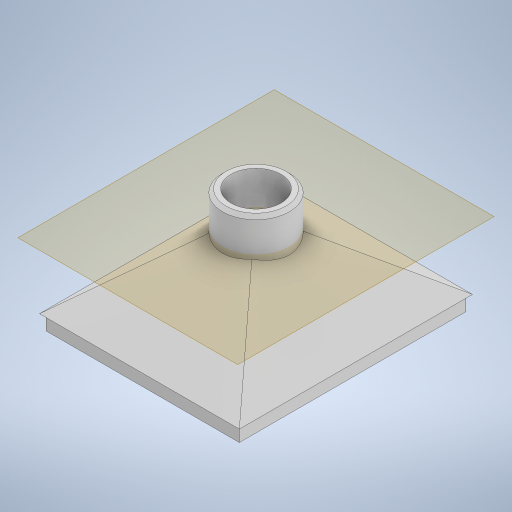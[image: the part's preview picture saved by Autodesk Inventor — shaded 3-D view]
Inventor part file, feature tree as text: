
AUTODESK INVENTOR PART (.ipt)
format: ipt  version: 2023 (Build 270158000, 158)  size: 410,624 bytes
history: native  units: mm
features: sketch x7, extrude x4, chamfer x2, plane x1, loft x1, hole x1, shell x1, fillet x1
ambient origin geometry x8: Origin, YZ Plane, XZ Plane, XY Plane, X Axis, Y Axis, Z Axis, Center Point
bodies: Solid1 (feature_tree)
feature tree (18):
  sketch  "Sketch1"  dims[d0=60.0mm d1=70.0mm]
  plane  "Work Plane1"
  loft  "Loft1"
  hole  "Hole1"  [1 undecoded]
  sketch  "Sketch10"  dims[d9=15.0mm d10=6.0mm d11=4.0mm d12=2.0mm d13=90.0deg d14=8.0mm d15=20.594885mm d16=1.0mm]
  shell  "Shell1"  Thickness=0.0mm
  extrude  "Extrusion1"  Depth=1.0mm
  extrude  "Extrusion2"  Depth=1.0mm
  fillet  "Fillet2"  Radius=1.0mm
  chamfer  "Chamfer1"  Distance=5.0mm
  extrude  "Extrusion3"  Depth=10.0mm
  extrude  "Extrusion4"  Depth=10.0mm
  chamfer  "Chamfer2"  Distance=1.0mm
  sketch  "Sketch2"  dims[d2=20.0mm d3=15.0mm d4=0.0mm d5=90.0deg]
  sketch  "Sketch6"  dims[d6=0.0mm d7=90.0deg]
  sketch  "Sketch12"  dims[d20=1.0mm d21=1.0mm d22=1.0mm]
  sketch  "Sketch13"  dims[d23=1.0mm d24=5.0mm d25=0.0mm]
  sketch  "Sketch14"  dims[d26=1.0mm d27=1.0mm d28=1.0mm d29=1.0mm d30=5.0mm d31=0.0mm d32=10.0mm d33=0.5mm d34=2.0mm d35=45.0deg d36=20.0mm d37=5.0mm d38=0.0mm d39=10.0mm d40=0.0mm d41=1.0mm d42=2.0mm d43=45.0deg]
note: 1 required parameter value undecoded (feature->parameter linkage not recoverable at this tier; creation-order binding heuristic only, values carry confidence <= 0.55)
